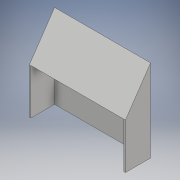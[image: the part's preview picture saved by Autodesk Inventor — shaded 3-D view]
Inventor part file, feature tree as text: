
AUTODESK INVENTOR PART (.ipt)
format: ipt  version: 2018.2 (Build 222227000, 227)  size: 130,048 bytes
history: native  units: mm
features: extrude x4, sketch x4
ambient origin geometry x8: Origin, YZ Plane, XZ Plane, XY Plane, X Axis, Y Axis, Z Axis, Center Point
bodies: Solid1 (feature_tree)
feature tree (8):
  extrude  "Extrusion1"  Depth=156.0mm
  extrude  "Extrusion2"  Depth=38.5mm
  extrude  "Extrusion3"  Depth=73.9mm TaperAngle=0.0deg
  extrude  "Extrusion4"  Depth=2.4mm TaperAngle=0.0deg
  sketch  "Sketch1"  dims[d0=40.9mm d1=156.0mm]
  sketch  "Sketch2"  dims[d2=2.4mm d3=38.5mm]
  sketch  "Sketch3"  dims[d4=151.2mm d5=73.9mm d6=0.0mm]
  sketch  "Sketch5"  dims[d8=2.4mm d9=0.0mm d10=2.4mm d11=0.0mm d12=60.0mm d13=2.4mm d14=156.0mm d15=0.0mm]
